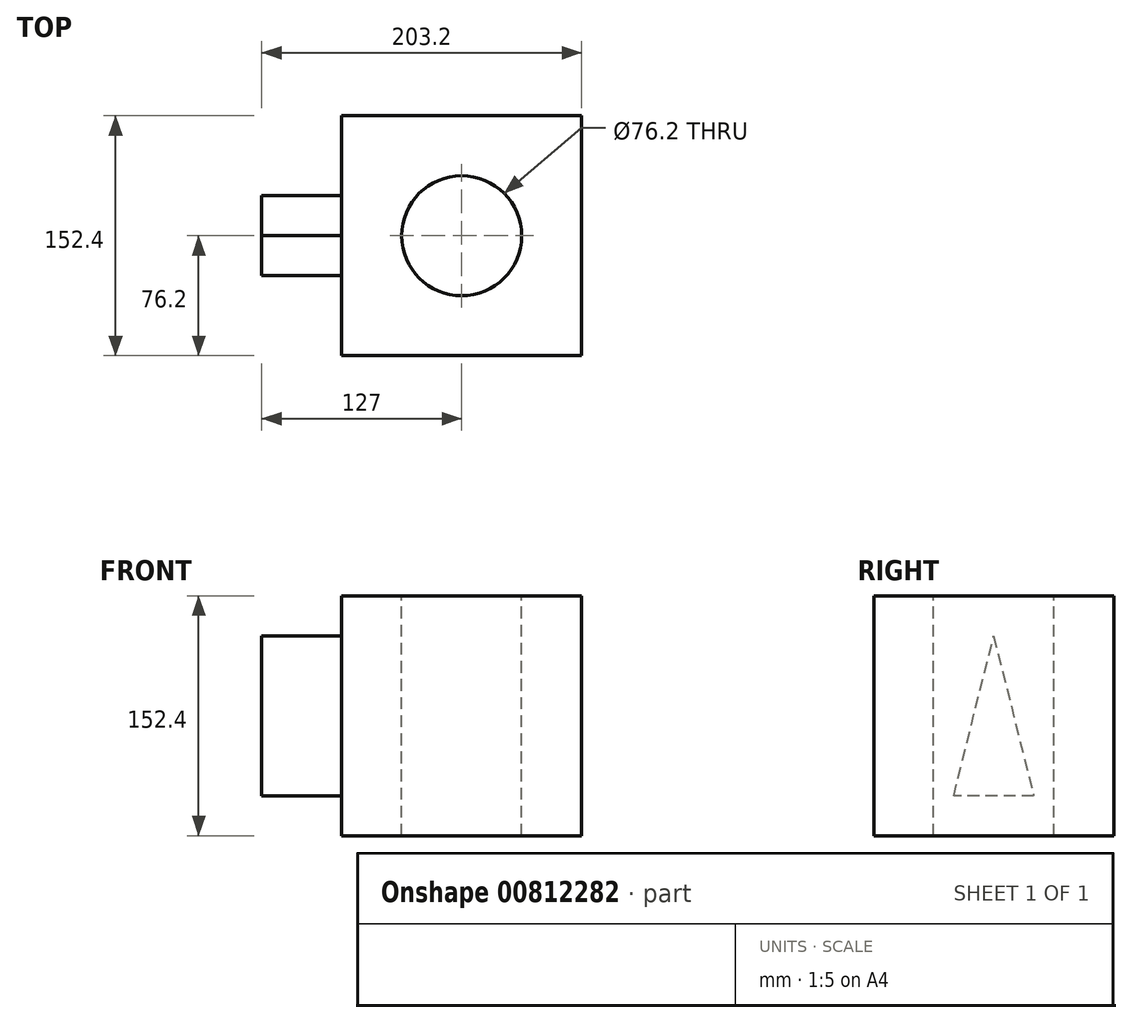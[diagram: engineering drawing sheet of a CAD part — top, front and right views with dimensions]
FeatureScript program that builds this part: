
annotation { "Feature Type Name" : "Feature", "Feature Type Description" : "" }
export const myFeature = defineFeature(function(context is Context, id is Id, definition is map)
    precondition{}
    {
        {
            var Q0;
            Q0=qCreatedBy(makeId("Top.planeOp"),FACE);
            var sketch = newSketch(context, id + "F0", { "sketchPlane" : qUnion([Q0])});
            skLineSegment(sketch, "E0.bottom", {"start": v(76.2, -76.2) * mm, "end": v(-76.2, -76.2) * mm});
            skLineSegment(sketch, "E0.top", {"start": v(76.2, 76.2) * mm, "end": v(-76.2, 76.2) * mm});
            skLineSegment(sketch, "E0.left", {"start": v(76.2, -76.2) * mm, "end": v(76.2, 76.2) * mm});
            skLineSegment(sketch, "E0.right", {"start": v(-76.2, -76.2) * mm, "end": v(-76.2, 76.2) * mm});
            skPoint(sketch, "E0.middle", {"position": v(0, 0) * mm});
            skSolve(sketch);
        }
        {
            var Q0;
            Q0 = qSketchRegion(id + "F0", true);
            extrude(context, id + "F1", {"entities" : qUnion([Q0]), "endBound" : BoundingType.SYMMETRIC, "depth" : 152.4 * mm, "offsetDistance" : 25.4 * mm});
        }
        {
            var Q0;
            Q0=makeQuery(id+"F1.opExtrude","CAP_FACE",FACE,{"disambiguationData":[OSD([sQuery(id+"F0.wireOp",EDGE,"E0.bottom"),sQuery(id+"F0.wireOp",EDGE,"E0.top"),sQuery(id+"F0.wireOp",EDGE,"E0.left"),sQuery(id+"F0.wireOp",EDGE,"E0.right")])],"isStart":false});
            var sketch = newSketch(context, id + "F2", { "sketchPlane" : qUnion([Q0])});
            skCircle(sketch, "E1", {"center": v(0, 0) * mm, "radius": 38.1 * mm});
            skSolve(sketch);
        }
        {
            var Q0;
            Q0 = qSketchRegion(id + "F2", true);
            extrude(context, id + "F3", {"entities" : qUnion([Q0]), "operationType" : NewBodyOperationType.REMOVE, "endBound" : BoundingType.THROUGH_ALL, "oppositeDirection" : true, "depth" : 25.4 * mm, "offsetDistance" : 25.4 * mm});
        }
        {
            var Q0;
            Q0=makeQuery(id+"F1.opExtrude","SWEPT_FACE",FACE,{"disambiguationData":[OSD([sQuery(id+"F0.wireOp",EDGE,"E0.right")])]});
            var sketch = newSketch(context, id + "F4", { "sketchPlane" : qUnion([Q0])});
            skLineSegment(sketch, "E2", {"start": v(-25.4, -50.8) * mm, "end": v(25.4, -50.8) * mm});
            skLineSegment(sketch, "E3", {"start": v(25.4, -50.8) * mm, "end": v(0, 50.8) * mm});
            skLineSegment(sketch, "E4", {"start": v(0, 50.8) * mm, "end": v(-25.4, -50.8) * mm});
            skLineSegment(sketch, "E5", {"start": v(0, -50.8) * mm, "end": v(0, 0) * mm, "construction": true});
            skSolve(sketch);
        }
        {
            var Q0;
            Q0 = qSketchRegion(id + "F4", true);
            extrude(context, id + "F5", {"entities" : qUnion([Q0]), "operationType" : NewBodyOperationType.ADD, "depth" : 50.8 * mm, "offsetDistance" : 25.4 * mm});
        }
    });
